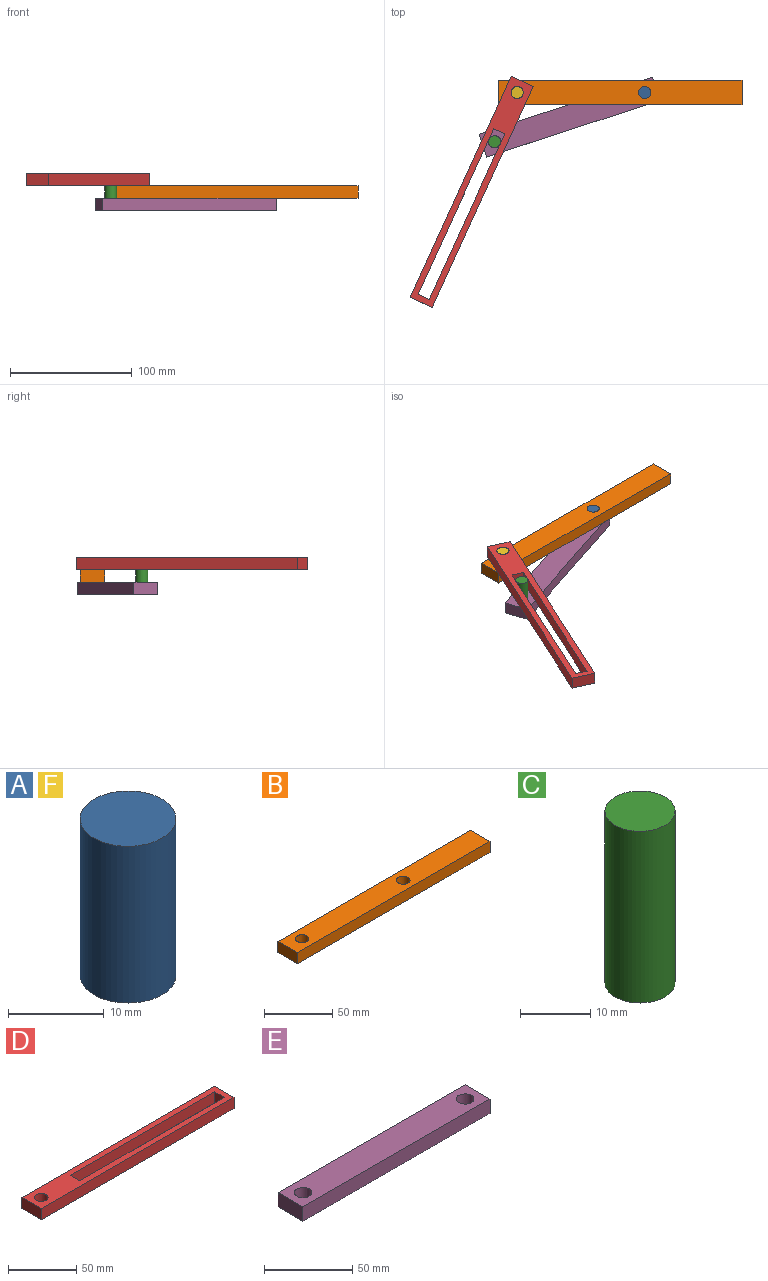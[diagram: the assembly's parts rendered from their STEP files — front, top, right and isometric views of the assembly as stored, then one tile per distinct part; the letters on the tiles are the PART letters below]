
ASSEMBLY  parts=6 mates=5
PART A: 3 faces, bbox 10x10x20 mm
  f0: cylinder r=5mm len=20mm, axis (0,0,-1), area 628.3mm2, adj f1,f2
  f1: plane 10x10mm, normal (0,0,1), area 78.5mm2, adj f0
  f2: plane 10x10mm, normal (0,0,-1), area 78.5mm2, adj f0
PART B: 8 faces, bbox 200x20x10 mm
  f0: plane 200x10mm, normal (0,-1,0), area 2000mm2, adj f1,f5,f6,f7
  f1: plane 20x10mm, normal (1,0,0), area 200mm2, adj f0,f2,f6,f7
  f2: plane 200x10mm, normal (0,1,0), area 2000mm2, adj f1,f5,f6,f7
  f3: cylinder r=5mm len=10mm, axis (0,0,-1), area 314.2mm2, adj f6,f7
  f4: cylinder r=5mm len=10mm, axis (0,0,-1), area 314.2mm2, adj f6,f7
  f5: plane 20x10mm, normal (-1,0,0), area 200mm2, adj f0,f2,f6,f7
  f6: plane 200x20mm, normal (0,0,1), area 3842.9mm2, adj f0,f1,f2,f3,f4,f5
  f7: plane 200x20mm, normal (0,0,-1), area 3842.9mm2, adj f0,f1,f2,f3,f4,f5
PART C: 3 faces, bbox 10x10x30 mm
  f0: cylinder r=5mm len=30mm, axis (0,0,-1), area 942.5mm2, adj f1,f2
  f1: plane 10x10mm, normal (0,0,1), area 78.5mm2, adj f0
  f2: plane 10x10mm, normal (0,0,-1), area 78.5mm2, adj f0
PART D: 11 faces, bbox 200x20x10 mm
  f0: plane 200x10mm, normal (0,-1,0), area 2000mm2, adj f1,f8,f9,f10
  f1: plane 20x10mm, normal (1,0,0), area 200mm2, adj f0,f2,f9,f10
  f2: plane 200x10mm, normal (0,1,0), area 2000mm2, adj f1,f8,f9,f10
  f3: plane 10x10mm, normal (-1,0,0), area 100mm2, adj f4,f6,f9,f10
  f4: plane 150x10mm, normal (0,1,0), area 1500mm2, adj f3,f5,f9,f10
  f5: plane 10x10mm, normal (1,0,0), area 100mm2, adj f4,f6,f9,f10
  f6: plane 150x10mm, normal (0,-1,0), area 1500mm2, adj f3,f5,f9,f10
  f7: cylinder r=5mm len=10mm, axis (0,0,-1), area 314.2mm2, adj f9,f10
  f8: plane 20x10mm, normal (-1,0,0), area 200mm2, adj f0,f2,f9,f10
  f9: plane 200x20mm, normal (0,0,1), area 2421.5mm2, adj f0,f1,f2,f3,f4,f5,f6,f7
  f10: plane 200x20mm, normal (0,0,-1), area 2421.5mm2, adj f0,f1,f2,f3,f4,f5,f6,f7
PART E: 8 faces, bbox 150x20x10 mm
  f0: plane 150x10mm, normal (0,-1,0), area 1500mm2, adj f1,f5,f6,f7
  f1: plane 20x10mm, normal (1,0,0), area 200mm2, adj f0,f2,f6,f7
  f2: plane 150x10mm, normal (0,1,0), area 1500mm2, adj f1,f5,f6,f7
  f3: cylinder r=5mm len=10mm, axis (0,0,-1), area 314.2mm2, adj f6,f7
  f4: cylinder r=5mm len=10mm, axis (0,0,-1), area 314.2mm2, adj f6,f7
  f5: plane 20x10mm, normal (-1,0,0), area 200mm2, adj f0,f2,f6,f7
  f6: plane 150x20mm, normal (0,0,1), area 2842.9mm2, adj f0,f1,f2,f3,f4,f5
  f7: plane 150x20mm, normal (0,0,-1), area 2842.9mm2, adj f0,f1,f2,f3,f4,f5
PART F: same geometry as A
PLACE A t=(105,0,-10)mm
PLACE B at identity fixed
PLACE C rot(axis=(0,0,-1),71.8deg) t=(-109.76,-21.51,-10)mm
PLACE D rot(axis=(0,0,-1),114.6deg) t=(-82.44,-100.13,10)mm
PLACE E rot(axis=(0,0,1),18.2deg) t=(-26.21,-67.67,-10)mm
PLACE F at identity fixed
MATE revolute F.f0 <-> D.f7  axis (0,0,1) through (-85,0,20)mm
MATE pin_slot C.f0 <-> D.f9  axis (0,0,1) through (-103.53,-40.51,20)mm
MATE fastened E.f3 <-> C.f0  axis (0,0,-1) through (-103.53,-40.51,-10)mm
MATE fastened A.f0 <-> B.f4  axis (0,0,1) through (20,0,10)mm
MATE revolute E.f4 <-> A.f0  axis (0,0,-1) through (20,0,-10)mm
